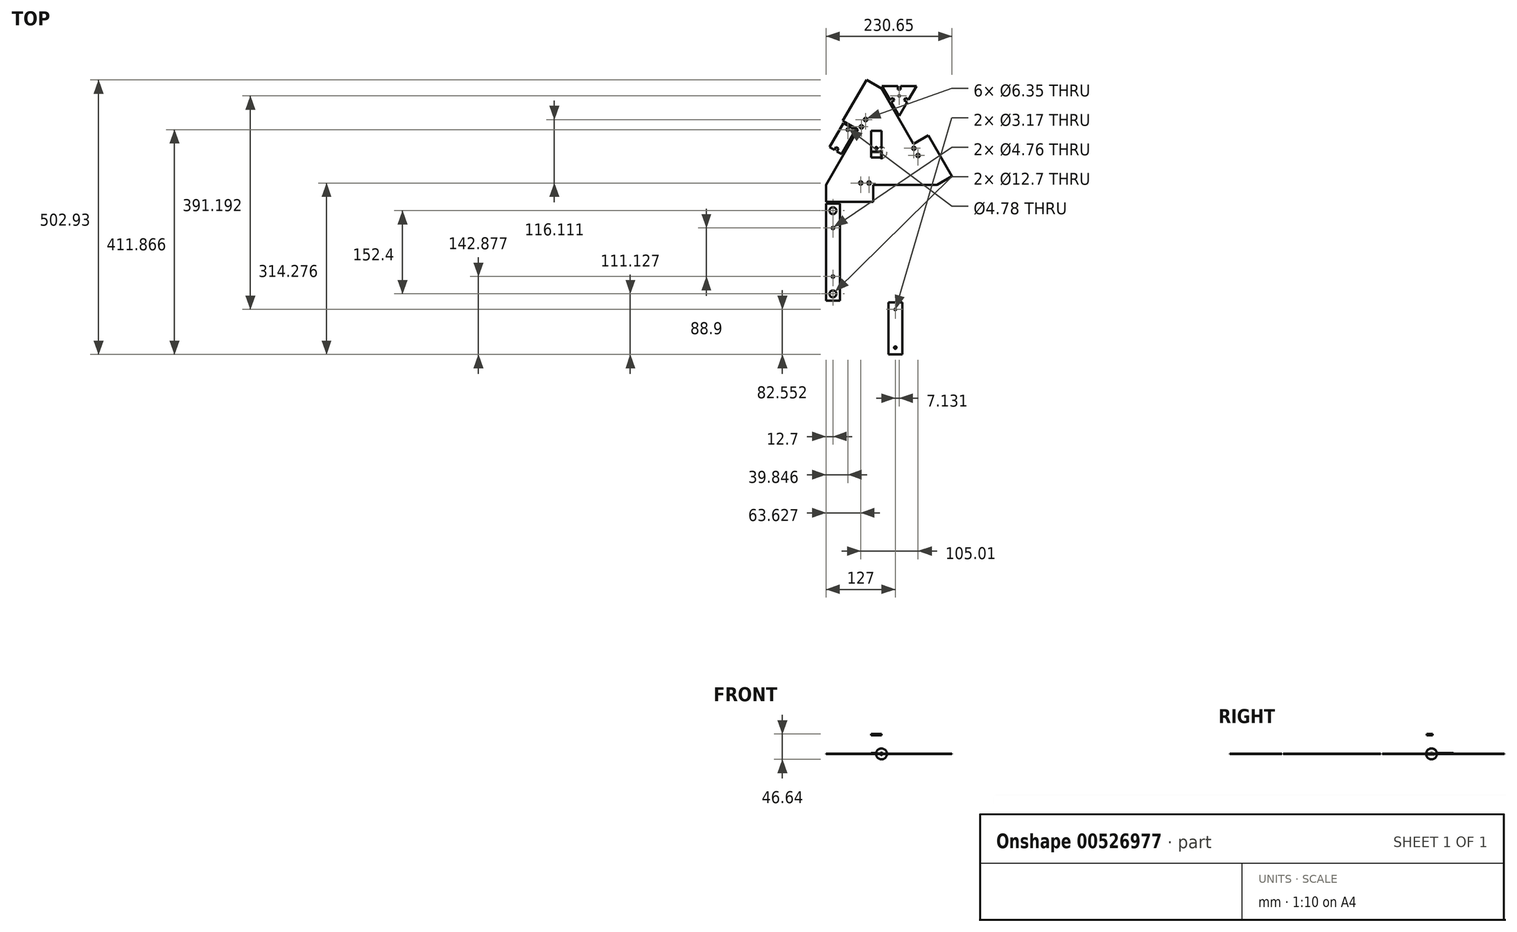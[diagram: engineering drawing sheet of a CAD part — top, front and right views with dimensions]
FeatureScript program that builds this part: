
annotation { "Feature Type Name" : "Feature", "Feature Type Description" : "" }
export const myFeature = defineFeature(function(context is Context, id is Id, definition is map)
    precondition{}
    {
        {
            assignVariable(context, id + "F0", {"name" : "ServoL", "anyValue" : 1.57});
        }
        {
            assignVariable(context, id + "F1", {"name" : "ServoW", "anyValue" : 1.7});
        }
        {
            assignVariable(context, id + "F2", {"name" : "ServoOffset", "anyValue" : .25});
        }
        {
            assignVariable(context, id + "F3", {"name" : "PlywoodThick", "anyValue" : .21});
        }
        {
            assignVariable(context, id + "F4", {"name" : "ScrewL", "anyValue" : 3});
        }
        {
            var Q0;
            Q0=qCreatedBy(makeId("Top.planeOp"),FACE);
            var sketch = newSketch(context, id + "F5", { "sketchPlane" : qUnion([Q0])});
            skCircle(sketch, "E0.cCircle", {"center": v(0, 0) * mm, "radius": 58.66 * mm, "construction": true});
            skLineSegment(sketch, "E0.0", {"start": v(101.6, -58.66) * mm, "end": v(0, -58.66) * mm});
            skLineSegment(sketch, "E0.1", {"start": v(-101.6, -58.66) * mm, "end": v(-50.8, 29.33) * mm});
            skLineSegment(sketch, "E0.2", {"start": v(0, 117.32) * mm, "end": v(50.8, 29.33) * mm});
            skPoint(sketch, "E0.0.midPoint", {"position": v(0, -58.66) * mm});
            skPoint(sketch, "E1", {"position": v(-50.8, 29.33) * mm});
            skPoint(sketch, "E2", {"position": v(50.8, 29.33) * mm});
            skLineSegment(sketch, "E3", {"start": v(-50.8, 29.33) * mm, "end": v(-43.24, 42.42) * mm});
            skLineSegment(sketch, "E4", {"start": v(50.8, 29.33) * mm, "end": v(58.36, 16.24) * mm});
            skLineSegment(sketch, "E5", {"start": v(0, -58.66) * mm, "end": v(-15.11, -58.66) * mm});
            skLineSegment(sketch, "E6", {"start": v(-40, -58.66) * mm, "end": v(-40, -3.67) * mm});
            skLineSegment(sketch, "E7", {"start": v(-40, -3.67) * mm, "end": v(40, -3.67) * mm});
            skLineSegment(sketch, "E8", {"start": v(40, -3.67) * mm, "end": v(40, -58.66) * mm});
            skPoint(sketch, "E9", {"position": v(0, -3.67) * mm});
            skLineSegment(sketch, "E10", {"start": v(-27.5, -3.67) * mm, "end": v(-27.5, 66.33) * mm});
            skLineSegment(sketch, "E11", {"start": v(-27.5, 66.33) * mm, "end": v(27.5, 66.33) * mm});
            skLineSegment(sketch, "E12", {"start": v(27.5, 66.33) * mm, "end": v(27.5, -3.67) * mm});
            skLineSegment(sketch, "E13", {"start": v(-15.11, -58.66) * mm, "end": v(-15.11, -58.66) * mm});
            skLineSegment(sketch, "E14", {"start": v(-15.11, -90.36) * mm, "end": v(-101.6, -90.36) * mm});
            skLineSegment(sketch, "E15", {"start": v(-101.6, -90.36) * mm, "end": v(-101.6, -58.66) * mm});
            skLineSegment(sketch, "E16.1.0", {"start": v(129.05, -42.8) * mm, "end": v(101.6, -58.66) * mm});
            skLineSegment(sketch, "E16.1.1", {"start": v(85.8, 32.1) * mm, "end": v(129.05, -42.8) * mm});
            skLineSegment(sketch, "E16.1.2", {"start": v(58.36, 16.24) * mm, "end": v(85.8, 32.1) * mm});
            skLineSegment(sketch, "E16.2.0", {"start": v(-27.45, 133.17) * mm, "end": v(0, 117.32) * mm});
            skLineSegment(sketch, "E16.2.1", {"start": v(-70.7, 58.27) * mm, "end": v(-27.45, 133.17) * mm});
            skLineSegment(sketch, "E16.2.2", {"start": v(-43.24, 42.42) * mm, "end": v(-43.24, 42.42) * mm});
            skLineSegment(sketch, "E17", {"start": v(-15.11, -58.66) * mm, "end": v(-15.11, -90.36) * mm});
            skLineSegment(sketch, "E18", {"start": v(-43.24, 42.42) * mm, "end": v(-70.7, 58.27) * mm});
            skLineSegment(sketch, "E19", {"start": v(58.36, 16.24) * mm, "end": v(101.6, -58.66) * mm, "construction": true});
            skLineSegment(sketch, "E20", {"start": v(-15.11, -58.66) * mm, "end": v(-101.6, -58.66) * mm, "construction": true});
            skLineSegment(sketch, "E21", {"start": v(-43.24, 42.42) * mm, "end": v(0, 117.32) * mm, "construction": true});
            skPoint(sketch, "E22", {"position": v(59.52, 20.58) * mm});
            skLineSegment(sketch, "E23", {"start": v(59.52, 20.58) * mm, "end": v(34.12, 64.57) * mm});
            skLineSegment(sketch, "E24", {"start": v(34.12, 64.57) * mm, "end": v(42.8, 69.59) * mm});
            skLineSegment(sketch, "E25", {"start": v(56.12, 77.27) * mm, "end": v(81.52, 33.28) * mm});
            skLineSegment(sketch, "E26", {"start": v(81.52, 33.28) * mm, "end": v(59.52, 20.58) * mm});
            skPoint(sketch, "E27", {"position": v(45.12, 70.92) * mm});
            skLineSegment(sketch, "E28", {"start": v(42.8, 69.59) * mm, "end": v(45.98, 64.09) * mm});
            skLineSegment(sketch, "E29", {"start": v(45.98, 64.09) * mm, "end": v(50.6, 66.76) * mm});
            skLineSegment(sketch, "E30", {"start": v(50.6, 66.76) * mm, "end": v(47.43, 72.26) * mm});
            skLineSegment(sketch, "E31", {"start": v(42.8, 69.59) * mm, "end": v(47.43, 72.26) * mm, "construction": true});
            skLineSegment(sketch, "E32", {"start": v(47.43, 72.26) * mm, "end": v(56.12, 77.27) * mm});
            skLineSegment(sketch, "E33.1.0", {"start": v(-47.58, 41.26) * mm, "end": v(-72.98, -2.74) * mm});
            skLineSegment(sketch, "E33.1.1", {"start": v(-72.98, -2.74) * mm, "end": v(-81.67, 2.28) * mm});
            skLineSegment(sketch, "E33.1.2", {"start": v(-81.67, 2.28) * mm, "end": v(-78.5, 7.78) * mm});
            skLineSegment(sketch, "E33.1.3", {"start": v(-78.5, 7.78) * mm, "end": v(-83.11, 10.44) * mm});
            skLineSegment(sketch, "E33.1.4", {"start": v(-83.11, 10.44) * mm, "end": v(-86.29, 4.94) * mm});
            skLineSegment(sketch, "E33.1.5", {"start": v(-86.29, 4.94) * mm, "end": v(-94.98, 9.96) * mm});
            skLineSegment(sketch, "E33.1.6", {"start": v(-94.98, 9.96) * mm, "end": v(-69.58, 53.96) * mm});
            skLineSegment(sketch, "E33.1.7", {"start": v(-81.67, 2.28) * mm, "end": v(-86.29, 4.94) * mm, "construction": true});
            skPoint(sketch, "E33.1.8", {"position": v(-83.98, 3.61) * mm});
            skLineSegment(sketch, "E33.1.9", {"start": v(-69.58, 53.96) * mm, "end": v(-47.58, 41.26) * mm});
            skLineSegment(sketch, "E33.2.0", {"start": v(-11.94, -61.83) * mm, "end": v(38.86, -61.83) * mm});
            skLineSegment(sketch, "E33.2.1", {"start": v(38.86, -61.83) * mm, "end": v(38.86, -71.87) * mm});
            skLineSegment(sketch, "E33.2.2", {"start": v(38.86, -71.87) * mm, "end": v(32.51, -71.87) * mm});
            skLineSegment(sketch, "E33.2.3", {"start": v(32.51, -71.87) * mm, "end": v(32.51, -77.2) * mm});
            skLineSegment(sketch, "E33.2.4", {"start": v(32.51, -77.2) * mm, "end": v(38.86, -77.2) * mm});
            skLineSegment(sketch, "E33.2.5", {"start": v(38.86, -77.2) * mm, "end": v(38.86, -87.23) * mm});
            skLineSegment(sketch, "E33.2.6", {"start": v(38.86, -87.23) * mm, "end": v(-11.94, -87.23) * mm});
            skLineSegment(sketch, "E33.2.7", {"start": v(38.86, -71.87) * mm, "end": v(38.86, -77.2) * mm, "construction": true});
            skPoint(sketch, "E33.2.8", {"position": v(38.86, -74.53) * mm});
            skLineSegment(sketch, "E33.2.9", {"start": v(-11.94, -87.23) * mm, "end": v(-11.94, -61.83) * mm});
            skLineSegment(sketch, "E34.bottom", {"start": v(-101.6, -93.53) * mm, "end": v(-76.2, -93.53) * mm});
            skLineSegment(sketch, "E34.top", {"start": v(-101.6, -271.33) * mm, "end": v(-76.2, -271.33) * mm});
            skLineSegment(sketch, "E34.left", {"start": v(-101.6, -93.53) * mm, "end": v(-101.6, -271.33) * mm});
            skLineSegment(sketch, "E34.right", {"start": v(-76.2, -93.53) * mm, "end": v(-76.2, -271.33) * mm});
            skCircle(sketch, "E35", {"center": v(-88.9, -258.63) * mm, "radius": 6.35 * mm});
            skPoint(sketch, "E35.centerSnap0", {"position": v(-88.9, -271.33) * mm});
            skCircle(sketch, "E36", {"center": v(-88.9, -106.23) * mm, "radius": 6.35 * mm});
            skPoint(sketch, "E36.centerSnap0", {"position": v(-88.9, -93.53) * mm});
            skCircle(sketch, "E37", {"center": v(-88.9, -226.88) * mm, "radius": 2.38 * mm});
            skCircle(sketch, "E38", {"center": v(-88.9, -137.98) * mm, "radius": 2.38 * mm});
            skLineSegment(sketch, "E39.1.0.0", {"start": v(-73.02, -93.53) * mm, "end": v(-73.02, -271.33) * mm});
            skLineSegment(sketch, "E39.1.0.1", {"start": v(-73.02, -93.53) * mm, "end": v(-47.62, -93.53) * mm});
            skLineSegment(sketch, "E39.1.0.2", {"start": v(-47.62, -93.53) * mm, "end": v(-47.62, -271.33) * mm});
            skCircle(sketch, "E39.1.0.3", {"center": v(-60.32, -106.23) * mm, "radius": 6.35 * mm});
            skCircle(sketch, "E39.1.0.4", {"center": v(-60.32, -137.98) * mm, "radius": 2.38 * mm});
            skCircle(sketch, "E39.1.0.5", {"center": v(-60.32, -226.88) * mm, "radius": 2.38 * mm});
            skCircle(sketch, "E39.1.0.6", {"center": v(-60.32, -258.63) * mm, "radius": 6.35 * mm});
            skLineSegment(sketch, "E39.1.0.7", {"start": v(-73.02, -271.33) * mm, "end": v(-47.62, -271.33) * mm});
            skLineSegment(sketch, "E39.2.0.0", {"start": v(-44.45, -93.53) * mm, "end": v(-44.45, -271.33) * mm});
            skLineSegment(sketch, "E39.2.0.1", {"start": v(-44.45, -93.53) * mm, "end": v(-19.05, -93.53) * mm});
            skLineSegment(sketch, "E39.2.0.2", {"start": v(-19.05, -93.53) * mm, "end": v(-19.05, -271.33) * mm});
            skCircle(sketch, "E39.2.0.3", {"center": v(-31.75, -106.23) * mm, "radius": 6.35 * mm});
            skCircle(sketch, "E39.2.0.4", {"center": v(-31.75, -137.98) * mm, "radius": 2.38 * mm});
            skCircle(sketch, "E39.2.0.5", {"center": v(-31.75, -226.88) * mm, "radius": 2.38 * mm});
            skCircle(sketch, "E39.2.0.6", {"center": v(-31.75, -258.63) * mm, "radius": 6.35 * mm});
            skLineSegment(sketch, "E39.2.0.7", {"start": v(-44.45, -271.33) * mm, "end": v(-19.05, -271.33) * mm});
            skLineSegment(sketch, "E39.3.0.0", {"start": v(-15.87, -93.53) * mm, "end": v(-15.87, -271.33) * mm});
            skLineSegment(sketch, "E39.3.0.1", {"start": v(-15.87, -93.53) * mm, "end": v(9.53, -93.53) * mm});
            skLineSegment(sketch, "E39.3.0.2", {"start": v(9.53, -93.53) * mm, "end": v(9.53, -271.33) * mm});
            skCircle(sketch, "E39.3.0.3", {"center": v(-3.17, -106.23) * mm, "radius": 6.35 * mm});
            skCircle(sketch, "E39.3.0.4", {"center": v(-3.17, -137.98) * mm, "radius": 2.38 * mm});
            skCircle(sketch, "E39.3.0.5", {"center": v(-3.17, -226.88) * mm, "radius": 2.38 * mm});
            skCircle(sketch, "E39.3.0.6", {"center": v(-3.17, -258.63) * mm, "radius": 6.35 * mm});
            skLineSegment(sketch, "E39.3.0.7", {"start": v(-15.87, -271.33) * mm, "end": v(9.53, -271.33) * mm});
            skLineSegment(sketch, "E39.4.0.0", {"start": v(12.7, -93.53) * mm, "end": v(12.7, -271.33) * mm});
            skLineSegment(sketch, "E39.4.0.1", {"start": v(12.7, -93.53) * mm, "end": v(38.1, -93.53) * mm});
            skLineSegment(sketch, "E39.4.0.2", {"start": v(38.1, -93.53) * mm, "end": v(38.1, -271.33) * mm});
            skCircle(sketch, "E39.4.0.3", {"center": v(25.4, -106.23) * mm, "radius": 6.35 * mm});
            skCircle(sketch, "E39.4.0.4", {"center": v(25.4, -137.98) * mm, "radius": 2.38 * mm});
            skCircle(sketch, "E39.4.0.5", {"center": v(25.4, -226.88) * mm, "radius": 2.38 * mm});
            skCircle(sketch, "E39.4.0.6", {"center": v(25.4, -258.63) * mm, "radius": 6.35 * mm});
            skLineSegment(sketch, "E39.4.0.7", {"start": v(12.7, -271.33) * mm, "end": v(38.1, -271.33) * mm});
            skLineSegment(sketch, "E39.5.0.0", {"start": v(41.28, -93.53) * mm, "end": v(41.28, -271.33) * mm});
            skLineSegment(sketch, "E39.5.0.1", {"start": v(41.28, -93.53) * mm, "end": v(66.68, -93.53) * mm});
            skLineSegment(sketch, "E39.5.0.2", {"start": v(66.68, -93.53) * mm, "end": v(66.68, -271.33) * mm});
            skCircle(sketch, "E39.5.0.3", {"center": v(53.98, -106.23) * mm, "radius": 6.35 * mm});
            skCircle(sketch, "E39.5.0.4", {"center": v(53.98, -137.98) * mm, "radius": 2.38 * mm});
            skCircle(sketch, "E39.5.0.5", {"center": v(53.98, -226.88) * mm, "radius": 2.38 * mm});
            skCircle(sketch, "E39.5.0.6", {"center": v(53.98, -258.63) * mm, "radius": 6.35 * mm});
            skLineSegment(sketch, "E39.5.0.7", {"start": v(41.28, -271.33) * mm, "end": v(66.68, -271.33) * mm});
            skLineSegment(sketch, "E39.6.0.0", {"start": v(69.85, -93.53) * mm, "end": v(69.85, -271.33) * mm});
            skLineSegment(sketch, "E39.6.0.1", {"start": v(69.85, -93.53) * mm, "end": v(95.25, -93.53) * mm});
            skLineSegment(sketch, "E39.6.0.2", {"start": v(95.25, -93.53) * mm, "end": v(95.25, -271.33) * mm});
            skCircle(sketch, "E39.6.0.3", {"center": v(82.55, -106.23) * mm, "radius": 6.35 * mm});
            skCircle(sketch, "E39.6.0.4", {"center": v(82.55, -137.98) * mm, "radius": 2.38 * mm});
            skCircle(sketch, "E39.6.0.5", {"center": v(82.55, -226.88) * mm, "radius": 2.38 * mm});
            skCircle(sketch, "E39.6.0.6", {"center": v(82.55, -258.63) * mm, "radius": 6.35 * mm});
            skLineSegment(sketch, "E39.6.0.7", {"start": v(69.85, -271.33) * mm, "end": v(95.25, -271.33) * mm});
            skLineSegment(sketch, "E39.7.0.0", {"start": v(98.43, -93.53) * mm, "end": v(98.43, -271.33) * mm});
            skLineSegment(sketch, "E39.7.0.1", {"start": v(98.43, -93.53) * mm, "end": v(123.83, -93.53) * mm});
            skLineSegment(sketch, "E39.7.0.2", {"start": v(123.83, -93.53) * mm, "end": v(123.83, -271.33) * mm});
            skCircle(sketch, "E39.7.0.3", {"center": v(111.13, -106.23) * mm, "radius": 6.35 * mm});
            skCircle(sketch, "E39.7.0.4", {"center": v(111.13, -137.98) * mm, "radius": 2.38 * mm});
            skCircle(sketch, "E39.7.0.5", {"center": v(111.13, -226.88) * mm, "radius": 2.38 * mm});
            skCircle(sketch, "E39.7.0.6", {"center": v(111.13, -258.63) * mm, "radius": 6.35 * mm});
            skLineSegment(sketch, "E39.7.0.7", {"start": v(98.43, -271.33) * mm, "end": v(123.83, -271.33) * mm});
            skLineSegment(sketch, "E39.direction1", {"start": v(-101.6, -271.33) * mm, "end": v(-73.02, -271.33) * mm, "construction": true});
            skLineSegment(sketch, "E40.bottom", {"start": v(-101.6, -274.5) * mm, "end": v(-76.2, -274.5) * mm});
            skLineSegment(sketch, "E40.top", {"start": v(-101.6, -452.3) * mm, "end": v(-76.2, -452.3) * mm});
            skLineSegment(sketch, "E40.left", {"start": v(-101.6, -274.5) * mm, "end": v(-101.6, -452.3) * mm});
            skLineSegment(sketch, "E40.right", {"start": v(-76.2, -274.5) * mm, "end": v(-76.2, -452.3) * mm});
            skCircle(sketch, "E41", {"center": v(-88.9, -439.6) * mm, "radius": 6.35 * mm});
            skPoint(sketch, "E41.centerSnap0", {"position": v(-88.9, -452.3) * mm});
            skCircle(sketch, "E42", {"center": v(-88.9, -287.2) * mm, "radius": 6.35 * mm});
            skCircle(sketch, "E43", {"center": v(-88.9, -407.86) * mm, "radius": 2.38 * mm});
            skCircle(sketch, "E44", {"center": v(-88.9, -318.96) * mm, "radius": 2.38 * mm});
            skPoint(sketch, "E45", {"position": v(-88.9, -274.5) * mm});
            skCircle(sketch, "E46.1.0.0", {"center": v(-60.32, -287.2) * mm, "radius": 6.35 * mm});
            skPoint(sketch, "E46.1.0.1", {"position": v(-60.32, -452.3) * mm});
            skCircle(sketch, "E46.1.0.2", {"center": v(-60.32, -318.96) * mm, "radius": 2.38 * mm});
            skLineSegment(sketch, "E46.1.0.3", {"start": v(-73.02, -274.5) * mm, "end": v(-47.62, -274.5) * mm});
            skLineSegment(sketch, "E46.1.0.4", {"start": v(-73.02, -452.3) * mm, "end": v(-47.62, -452.3) * mm});
            skLineSegment(sketch, "E46.1.0.5", {"start": v(-73.02, -274.5) * mm, "end": v(-73.02, -452.3) * mm});
            skLineSegment(sketch, "E46.1.0.6", {"start": v(-47.62, -274.5) * mm, "end": v(-47.62, -452.3) * mm});
            skCircle(sketch, "E46.1.0.7", {"center": v(-60.32, -439.6) * mm, "radius": 6.35 * mm});
            skPoint(sketch, "E46.1.0.8", {"position": v(-60.32, -274.5) * mm});
            skCircle(sketch, "E46.1.0.9", {"center": v(-60.32, -407.86) * mm, "radius": 2.38 * mm});
            skPoint(sketch, "E46.1.0.10", {"position": v(-60.32, -271.33) * mm});
            skCircle(sketch, "E46.2.0.0", {"center": v(-31.75, -287.2) * mm, "radius": 6.35 * mm});
            skPoint(sketch, "E46.2.0.1", {"position": v(-31.75, -452.3) * mm});
            skCircle(sketch, "E46.2.0.2", {"center": v(-31.75, -318.96) * mm, "radius": 2.38 * mm});
            skLineSegment(sketch, "E46.2.0.3", {"start": v(-44.45, -274.5) * mm, "end": v(-19.05, -274.5) * mm});
            skLineSegment(sketch, "E46.2.0.4", {"start": v(-44.45, -452.3) * mm, "end": v(-19.05, -452.3) * mm});
            skLineSegment(sketch, "E46.2.0.5", {"start": v(-44.45, -274.5) * mm, "end": v(-44.45, -452.3) * mm});
            skLineSegment(sketch, "E46.2.0.6", {"start": v(-19.05, -274.5) * mm, "end": v(-19.05, -452.3) * mm});
            skCircle(sketch, "E46.2.0.7", {"center": v(-31.75, -439.6) * mm, "radius": 6.35 * mm});
            skPoint(sketch, "E46.2.0.8", {"position": v(-31.75, -274.5) * mm});
            skCircle(sketch, "E46.2.0.9", {"center": v(-31.75, -407.86) * mm, "radius": 2.38 * mm});
            skPoint(sketch, "E46.2.0.10", {"position": v(-31.75, -271.33) * mm});
            skCircle(sketch, "E46.3.0.0", {"center": v(-3.17, -287.2) * mm, "radius": 6.35 * mm});
            skPoint(sketch, "E46.3.0.1", {"position": v(-3.17, -452.3) * mm});
            skCircle(sketch, "E46.3.0.2", {"center": v(-3.17, -318.96) * mm, "radius": 2.38 * mm});
            skLineSegment(sketch, "E46.3.0.3", {"start": v(-15.87, -274.5) * mm, "end": v(9.53, -274.5) * mm});
            skLineSegment(sketch, "E46.3.0.4", {"start": v(-15.87, -452.3) * mm, "end": v(9.53, -452.3) * mm});
            skLineSegment(sketch, "E46.3.0.5", {"start": v(-15.87, -274.5) * mm, "end": v(-15.87, -452.3) * mm});
            skLineSegment(sketch, "E46.3.0.6", {"start": v(9.53, -274.5) * mm, "end": v(9.53, -452.3) * mm});
            skCircle(sketch, "E46.3.0.7", {"center": v(-3.17, -439.6) * mm, "radius": 6.35 * mm});
            skPoint(sketch, "E46.3.0.8", {"position": v(-3.17, -274.5) * mm});
            skCircle(sketch, "E46.3.0.9", {"center": v(-3.17, -407.86) * mm, "radius": 2.38 * mm});
            skPoint(sketch, "E46.3.0.10", {"position": v(-3.17, -271.33) * mm});
            skLineSegment(sketch, "E46.direction1", {"start": v(-101.6, -452.3) * mm, "end": v(-73.02, -452.3) * mm, "construction": true});
            skLineSegment(sketch, "E47.bottom", {"start": v(12.7, -274.5) * mm, "end": v(38.1, -274.5) * mm});
            skLineSegment(sketch, "E47.top", {"start": v(12.7, -369.76) * mm, "end": v(38.1, -369.76) * mm});
            skLineSegment(sketch, "E47.left", {"start": v(12.7, -274.5) * mm, "end": v(12.7, -369.76) * mm});
            skLineSegment(sketch, "E47.right", {"start": v(38.1, -274.5) * mm, "end": v(38.1, -369.76) * mm});
            skCircle(sketch, "E48", {"center": v(25.4, -287.2) * mm, "radius": 1.59 * mm});
            skPoint(sketch, "E48.centerSnap0", {"position": v(25.4, -274.5) * mm});
            skCircle(sketch, "E49", {"center": v(25.4, -357.06) * mm, "radius": 2.26 * mm});
            skPoint(sketch, "E49.centerSnap0", {"position": v(25.4, -369.76) * mm});
            skPoint(sketch, "E50.1.0.0", {"position": v(53.98, -369.76) * mm});
            skCircle(sketch, "E50.1.0.1", {"center": v(53.98, -357.06) * mm, "radius": 2.26 * mm});
            skLineSegment(sketch, "E50.1.0.2", {"start": v(41.28, -274.5) * mm, "end": v(66.68, -274.5) * mm});
            skPoint(sketch, "E50.1.0.3", {"position": v(53.98, -274.5) * mm});
            skLineSegment(sketch, "E50.1.0.4", {"start": v(41.28, -369.76) * mm, "end": v(66.68, -369.76) * mm});
            skLineSegment(sketch, "E50.1.0.5", {"start": v(41.28, -274.5) * mm, "end": v(41.28, -369.76) * mm});
            skLineSegment(sketch, "E50.1.0.6", {"start": v(66.68, -274.5) * mm, "end": v(66.68, -369.76) * mm});
            skCircle(sketch, "E50.1.0.7", {"center": v(53.98, -287.2) * mm, "radius": 1.59 * mm});
            skPoint(sketch, "E50.2.0.0", {"position": v(82.55, -369.76) * mm});
            skCircle(sketch, "E50.2.0.1", {"center": v(82.55, -357.06) * mm, "radius": 2.26 * mm});
            skLineSegment(sketch, "E50.2.0.2", {"start": v(69.85, -274.5) * mm, "end": v(95.25, -274.5) * mm});
            skPoint(sketch, "E50.2.0.3", {"position": v(82.55, -274.5) * mm});
            skLineSegment(sketch, "E50.2.0.4", {"start": v(69.85, -369.76) * mm, "end": v(95.25, -369.76) * mm});
            skLineSegment(sketch, "E50.2.0.5", {"start": v(69.85, -274.5) * mm, "end": v(69.85, -369.76) * mm});
            skLineSegment(sketch, "E50.2.0.6", {"start": v(95.25, -274.5) * mm, "end": v(95.25, -369.76) * mm});
            skCircle(sketch, "E50.2.0.7", {"center": v(82.55, -287.2) * mm, "radius": 1.59 * mm});
            skLineSegment(sketch, "E50.direction1", {"start": v(12.7, -369.76) * mm, "end": v(41.28, -369.76) * mm, "construction": true});
            skCircle(sketch, "E51.cCircle", {"center": v(32.53, 103.98) * mm, "radius": 18.33 * mm, "construction": true});
            skLineSegment(sketch, "E51.0", {"start": v(0.78, 122.31) * mm, "end": v(29.86, 122.31) * mm});
            skLineSegment(sketch, "E51.1", {"start": v(64.28, 122.31) * mm, "end": v(49.74, 97.13) * mm});
            skLineSegment(sketch, "E51.2", {"start": v(32.53, 67.32) * mm, "end": v(17.99, 92.5) * mm});
            skPoint(sketch, "E51.0.midPoint", {"position": v(32.53, 122.31) * mm});
            skPoint(sketch, "E52", {"position": v(16.66, 94.82) * mm});
            skPoint(sketch, "E53", {"position": v(48.4, 94.82) * mm});
            skLineSegment(sketch, "E54", {"start": v(16.66, 94.82) * mm, "end": v(15.32, 97.13) * mm, "construction": true});
            skLineSegment(sketch, "E55", {"start": v(48.4, 94.82) * mm, "end": v(47.07, 92.5) * mm, "construction": true});
            skLineSegment(sketch, "E56", {"start": v(32.53, 122.31) * mm, "end": v(32.53, 122.31) * mm});
            skLineSegment(sketch, "E57", {"start": v(32.53, 122.31) * mm, "end": v(35.2, 122.31) * mm, "construction": true});
            skLineSegment(sketch, "E58", {"start": v(17.99, 92.5) * mm, "end": v(23.49, 95.68) * mm});
            skLineSegment(sketch, "E59", {"start": v(23.49, 95.68) * mm, "end": v(20.82, 100.3) * mm});
            skLineSegment(sketch, "E60", {"start": v(20.82, 100.3) * mm, "end": v(15.32, 97.13) * mm});
            skLineSegment(sketch, "E61.1.0", {"start": v(41.57, 95.68) * mm, "end": v(47.07, 92.5) * mm});
            skLineSegment(sketch, "E61.1.1", {"start": v(44.24, 100.3) * mm, "end": v(41.57, 95.68) * mm});
            skLineSegment(sketch, "E61.1.2", {"start": v(49.74, 97.13) * mm, "end": v(44.24, 100.3) * mm});
            skLineSegment(sketch, "E61.2.0", {"start": v(35.2, 115.96) * mm, "end": v(35.2, 122.31) * mm});
            skLineSegment(sketch, "E61.2.1", {"start": v(29.86, 115.96) * mm, "end": v(35.2, 115.96) * mm});
            skLineSegment(sketch, "E61.2.2", {"start": v(29.86, 122.31) * mm, "end": v(29.86, 115.96) * mm});
            skLineSegment(sketch, "E62", {"start": v(29.86, 122.31) * mm, "end": v(32.53, 122.31) * mm, "construction": true});
            skLineSegment(sketch, "E63", {"start": v(35.2, 122.31) * mm, "end": v(64.28, 122.31) * mm});
            skLineSegment(sketch, "E64", {"start": v(15.32, 97.13) * mm, "end": v(0.78, 122.31) * mm});
            skLineSegment(sketch, "E65", {"start": v(17.99, 92.5) * mm, "end": v(16.66, 94.82) * mm, "construction": true});
            skLineSegment(sketch, "E66", {"start": v(47.07, 92.5) * mm, "end": v(32.53, 67.32) * mm});
            skLineSegment(sketch, "E67", {"start": v(49.74, 97.13) * mm, "end": v(48.4, 94.82) * mm, "construction": true});
            skCircle(sketch, "E68", {"center": v(32.53, 103.98) * mm, "radius": 1.59 * mm});
            skCircle(sketch, "E69", {"center": v(-22.73, -55.48) * mm, "radius": 3.18 * mm});
            skCircle(sketch, "E70", {"center": v(-37.97, -55.48) * mm, "radius": 3.18 * mm});
            skPoint(sketch, "E71", {"position": v(-22.73, -58.66) * mm});
            skPoint(sketch, "E72", {"position": v(-37.97, -58.66) * mm});
            skCircle(sketch, "E73.1.0", {"center": v(67.04, -5.14) * mm, "radius": 3.18 * mm});
            skCircle(sketch, "E73.1.1", {"center": v(59.42, 8.05) * mm, "radius": 3.18 * mm});
            skPoint(sketch, "E73.1.2", {"position": v(69.79, -3.56) * mm});
            skPoint(sketch, "E73.1.3", {"position": v(62.17, 9.64) * mm});
            skCircle(sketch, "E73.2.0", {"center": v(-29.06, 60.63) * mm, "radius": 3.18 * mm});
            skCircle(sketch, "E73.2.1", {"center": v(-36.68, 47.43) * mm, "radius": 3.18 * mm});
            skPoint(sketch, "E73.2.2", {"position": v(-31.81, 62.21) * mm});
            skPoint(sketch, "E73.2.3", {"position": v(-39.43, 49.02) * mm});
            skLineSegment(sketch, "E74", {"start": v(-27.45, 133.17) * mm, "end": v(64.28, 133.17) * mm, "construction": true});
            skCircle(sketch, "E75", {"center": v(-5.59, -74.53) * mm, "radius": 2.39 * mm});
            skPoint(sketch, "E75.centerSnap0", {"position": v(-11.94, -74.53) * mm});
            skCircle(sketch, "E76.1.0", {"center": v(67.34, 32.43) * mm, "radius": 2.39 * mm});
            skCircle(sketch, "E76.2.0", {"center": v(-61.75, 42.1) * mm, "radius": 2.39 * mm});
            skPoint(sketch, "E77", {"position": v(70.52, 26.93) * mm});
            skSolve(sketch);
        }
        {
            var Q0;
            Q0=qCreatedBy(makeId("Top.planeOp"),FACE);
            var sketch = newSketch(context, id + "F6", { "sketchPlane" : qUnion([Q0])});
            skCircle(sketch, "E78", {"center": v(0, 0) * mm, "radius": 10 * mm});
            skLineSegment(sketch, "E79", {"start": v(0, 10) * mm, "end": v(0, -10) * mm, "construction": true});
            skLineSegment(sketch, "E80", {"start": v(-2, 9.8) * mm, "end": v(-2, -9.8) * mm});
            skSolve(sketch);
        }
        {
            var Q0;
            {var subQ0=sQuery(id+"F6.wireOp",EDGE,"E80");Q0=makeQuery(id+"F6.imprint","IMPRINT",FACE,{"disambiguationData":[TD([[makeQuery(id+"F6.imprint","IMPRINT",EDGE,{"derivedFrom":subQ0}),-1.0]])]});}
            var Q1;
            Q1=sQuery(id+"F6.wireOp",EDGE,"E79");
            revolve(context, id + "F7", {"entities" : qUnion([Q0]), "axis" : qUnion([Q1]), "revolveType" : RevolveType.FULL});
        }
        {
            var Q0;
            Q0=makeQuery(id+"F5.imprint","IMPRINT",FACE,{"disambiguationData":[TD([[makeQuery(id+"F5.imprint","IMPRINT",EDGE,{"derivedFrom":sQuery(id+"F5.wireOp",EDGE,"E0.1")}),-1.0]])]});
            var Q1;
            {var subQ0=sQuery(id+"F5.wireOp",EDGE,"E10");Q1=makeQuery(id+"F5.imprint","IMPRINT",FACE,{"disambiguationData":[TD([[makeQuery(id+"F5.imprint","IMPRINT",EDGE,{"derivedFrom":subQ0}),-1.0]])]});}
            var Q2;
            Q2=makeQuery(id+"F5.imprint","IMPRINT",FACE,{"disambiguationData":[TD([[makeQuery(id+"F5.imprint","IMPRINT",EDGE,{"derivedFrom":sQuery(id+"F5.wireOp",EDGE,"E33.1.0")}),-1.0]])]});
            var Q3;
            Q3=makeQuery(id+"F5.imprint","IMPRINT",FACE,{"disambiguationData":[TD([[makeQuery(id+"F5.imprint","IMPRINT",EDGE,{"derivedFrom":sQuery(id+"F5.wireOp",EDGE,"E51.0")}),-1.0]])]});
            var Q4;
            Q4=makeQuery(id+"F5.imprint","IMPRINT",FACE,{"disambiguationData":[TD([[makeQuery(id+"F5.imprint","IMPRINT",EDGE,{"derivedFrom":sQuery(id+"F5.wireOp",EDGE,"E34.bottom")}),-1.0]])]});
            var Q5;
            Q5=makeQuery(id+"F5.imprint","IMPRINT",FACE,{"disambiguationData":[TD([[makeQuery(id+"F5.imprint","IMPRINT",EDGE,{"derivedFrom":sQuery(id+"F5.wireOp",EDGE,"E47.bottom")}),-1.0]])]});
            extrude(context, id + "F8", {"entities" : qUnion([Q0, Q1, Q2, Q3, Q4, Q5]), "depth" : (getVariable(context, 'PlywoodThick')) * mm, "offsetDistance" : 25.4 * mm});
        }
        {
            var Q0;
            Q0=qCreatedBy(makeId("Top.planeOp"),FACE);
            var sketch = newSketch(context, id + "F9", { "sketchPlane" : qUnion([Q0])});
            skCircle(sketch, "E81", {"center": v(0, 0) * mm, "radius": 2 * mm});
            skSolve(sketch);
        }
        {
            var Q0;
            Q0 = qSketchRegion(id + "F9", true);
            extrude(context, id + "F10", {"entities" : qUnion([Q0]), "depth" : (getVariable(context, 'ScrewL')) * mm, "offsetDistance" : 25.4 * mm});
        }
        {
            var Q0;
            Q0=qCreatedBy(makeId("Top.planeOp"),FACE);
            var sketch = newSketch(context, id + "F11", { "sketchPlane" : qUnion([Q0])});
            skLineSegment(sketch, "E82.bottom", {"start": v(0, 0) * mm, "end": v(-19, 0) * mm});
            skLineSegment(sketch, "E82.top", {"start": v(0, 40) * mm, "end": v(-19, 40) * mm});
            skLineSegment(sketch, "E82.left", {"start": v(0, 0) * mm, "end": v(0, 40) * mm});
            skLineSegment(sketch, "E82.right", {"start": v(-19, 0) * mm, "end": v(-19, 40) * mm});
            skCircle(sketch, "E83", {"center": v(-9.5, 8.26) * mm, "radius": 2 * mm});
            skPoint(sketch, "E83.centerSnap0", {"position": v(-9.5, 40) * mm});
            skSolve(sketch);
        }
        {
            var Q0;
            Q0=makeQuery(id+"F11.imprint","IMPRINT",FACE,{"disambiguationData":[TD([[makeQuery(id+"F11.imprint","IMPRINT",EDGE,{"derivedFrom":sQuery(id+"F11.wireOp",EDGE,"E82.bottom")}),-1.0]])]});
            extrude(context, id + "F12", {"entities" : qUnion([Q0]), "depth" : (getVariable(context, 'ServoW')) * mm, "offsetDistance" : 25.4 * mm});
        }
        {
            var Q0;
            Q0=makeQuery(id+"F11.imprint","IMPRINT",FACE,{"disambiguationData":[TD([[makeQuery(id+"F11.imprint","IMPRINT",EDGE,{"derivedFrom":sQuery(id+"F11.wireOp",EDGE,"E83")}),1.0]])]});
            extrude(context, id + "F13", {"entities" : qUnion([Q0]), "operationType" : NewBodyOperationType.ADD, "depth" : (getVariable(context, 'ServoW') + getVariable(context, 'ServoOffset')) * mm, "offsetDistance" : 25.4 * mm});
        }
        {
            var Q0;
            Q0=makeQuery(id+"F12.opExtrude","SWEPT_FACE",FACE,{"disambiguationData":[OSD([sQuery(id+"F11.wireOp",EDGE,"E82.bottom")])]});
            var sketch = newSketch(context, id + "F14", { "sketchPlane" : qUnion([Q0])});
            skLineSegment(sketch, "E84.bottom", {"start": v(-19, 36.65) * mm, "end": v(0, 36.65) * mm});
            skLineSegment(sketch, "E84.top", {"start": v(-19, 33.8) * mm, "end": v(0, 33.8) * mm});
            skLineSegment(sketch, "E84.left", {"start": v(-19, 36.65) * mm, "end": v(-19, 33.8) * mm});
            skLineSegment(sketch, "E84.right", {"start": v(0, 36.65) * mm, "end": v(0, 33.8) * mm});
            skSolve(sketch);
        }
        {
            var Q0;
            Q0=makeQuery(id+"F14.imprint","IMPRINT",FACE,{"disambiguationData":[TD([[makeQuery(id+"F14.imprint","IMPRINT",EDGE,{"derivedFrom":sQuery(id+"F14.wireOp",EDGE,"E84.bottom")}),-1.0]])]});
            extrude(context, id + "F15", {"entities" : qUnion([Q0]), "operationType" : NewBodyOperationType.ADD, "depth" : 8.76 * mm, "offsetDistance" : 25.4 * mm, "hasSecondDirection" : true, "secondDirectionOppositeDirection" : true, "secondDirectionDepth" : (getVariable(context, 'ServoL') + .345) * mm});
        }
    });
